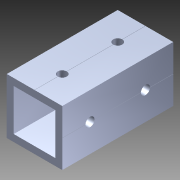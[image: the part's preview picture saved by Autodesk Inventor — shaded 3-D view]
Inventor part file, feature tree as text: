
AUTODESK INVENTOR PART (.ipt)
format: ipt  version: 2014 (Build 180170000, 170)  size: 1,106,944 bytes
history: native  units: in
note: dims shown in document units (in); Inventor stores cm internally (conversion verified against a paired STEP export)
features: pattern_circular x1, other x1, plane x1, extrude x1, imported_body x1, sketch x1
ambient origin geometry x8: Origin, YZ Plane, XZ Plane, XY Plane, X Axis, Y Axis, Z Axis, Center Point
bodies: Body1 (feature_tree)
feature tree (6):
  pattern_circular  "CirPattern2"
  other  "217-3426-STEP1"
  plane  "Work Plane1"
  extrude  "Extrusion1"  Depth=3937.0079in TaperAngle=0.0deg
  imported_body  "Base1"
  sketch  "Sketch1"  dims[d0=-2.0in d1=3937.0079in d2=0.0in]
